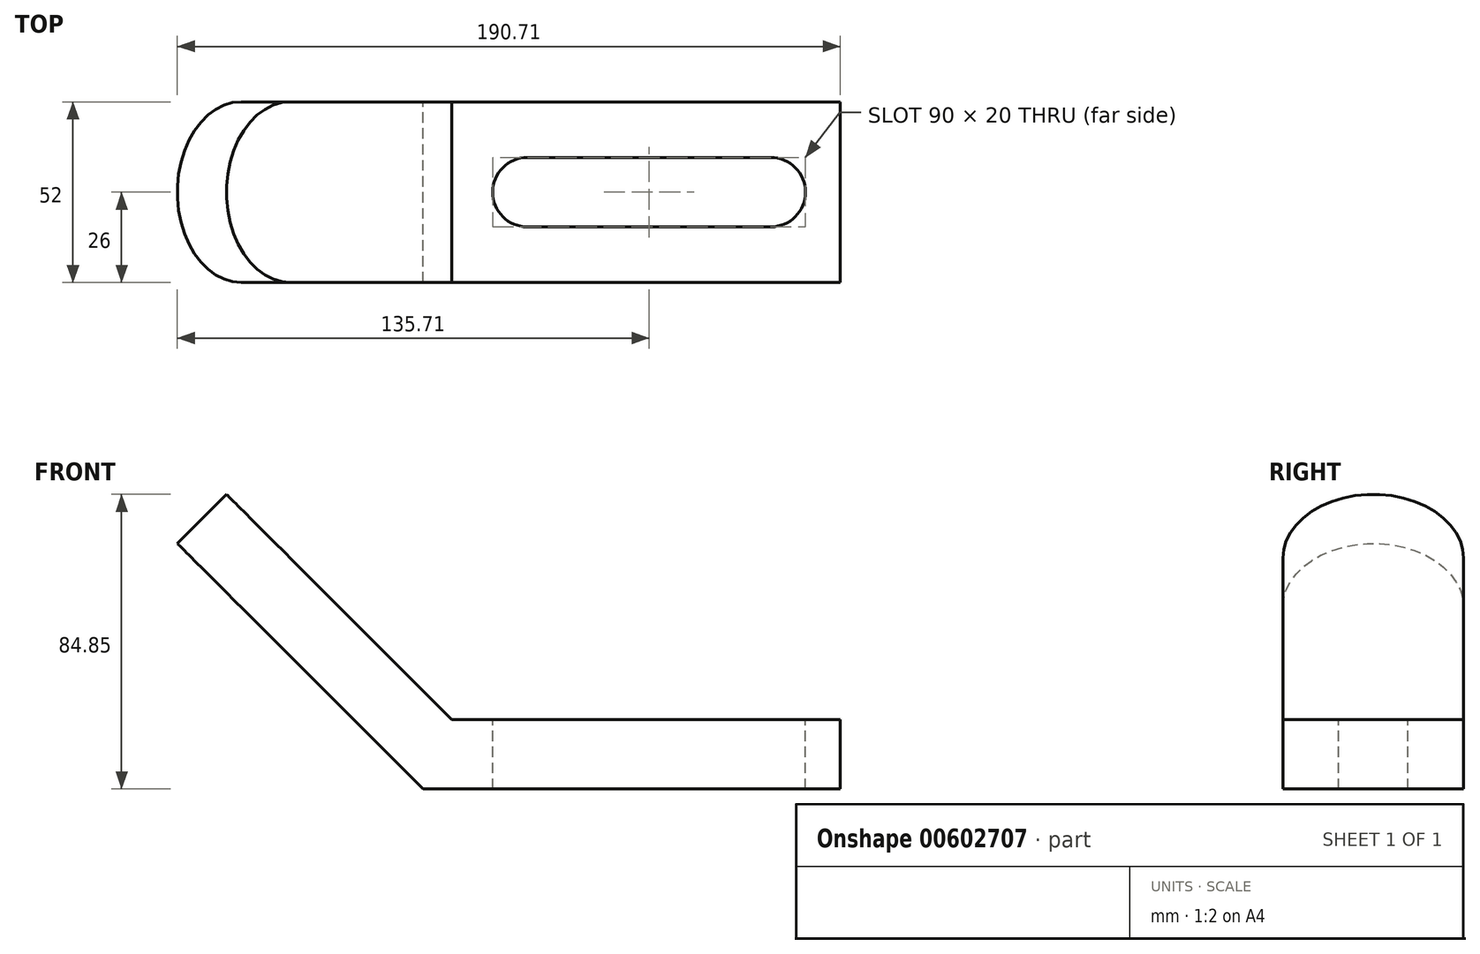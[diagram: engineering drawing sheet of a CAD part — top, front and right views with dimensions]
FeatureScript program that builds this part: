
annotation { "Feature Type Name" : "Feature", "Feature Type Description" : "" }
export const myFeature = defineFeature(function(context is Context, id is Id, definition is map)
    precondition{}
    {
        {
            var Q0;
            Q0=qCreatedBy(makeId("Front.planeOp"),FACE);
            var sketch = newSketch(context, id + "F0", { "sketchPlane" : qUnion([Q0])});
            skLineSegment(sketch, "E0", {"start": v(0, 0) * mm, "end": v(120, 0) * mm});
            skLineSegment(sketch, "E1", {"start": v(0, 0) * mm, "end": v(-70.71, 70.71) * mm});
            skLineSegment(sketch, "E2", {"start": v(-70.71, 70.71) * mm, "end": v(-56.57, 84.85) * mm});
            skLineSegment(sketch, "E3", {"start": v(-56.57, 84.85) * mm, "end": v(8.28, 20) * mm});
            skLineSegment(sketch, "E4", {"start": v(120, 0) * mm, "end": v(120, 20) * mm});
            skLineSegment(sketch, "E5", {"start": v(120, 20) * mm, "end": v(8.28, 20) * mm});
            skLineSegment(sketch, "E6", {"start": v(-45.25, 73.54) * mm, "end": v(-59.4, 59.4) * mm});
            skLineSegment(sketch, "E7", {"start": v(-31.11, 59.4) * mm, "end": v(-45.25, 45.25) * mm});
            skLineSegment(sketch, "E8", {"start": v(20, 20) * mm, "end": v(20, 0) * mm});
            skLineSegment(sketch, "E9", {"start": v(110, 20) * mm, "end": v(110, 0) * mm});
            skSolve(sketch);
        }
        {
            var Q0;
            Q0 = qSketchRegion(id + "F0", true);
            extrude(context, id + "F1", {"entities" : qUnion([Q0]), "depth" : 52 * mm, "offsetDistance" : 25 * mm});
        }
        {
            var Q0;
            Q0=makeQuery(id+"F1.opExtrude","CAP_EDGE",EDGE,{"disambiguationData":[OSD([sQuery(id+"F0.wireOp",EDGE,"E2")])],"isStart":true});
            var Q1;
            Q1=makeQuery(id+"F1.opExtrude","CAP_EDGE",EDGE,{"disambiguationData":[OSD([sQuery(id+"F0.wireOp",EDGE,"E2")])],"isStart":false});
            fillet(context, id + "F2", {"entities" : qUnion([Q0, Q1]), "radius" : 26 * mm, "tangentPropagation" : true, "allowEdgeOverflow" : false});
        }
        {
            var Q0;
            Q0=makeQuery(id+"F1.opExtrude","SWEPT_FACE",FACE,{"disambiguationData":[OSD([sQuery(id+"F0.wireOp",EDGE,"E3")])]});
            var sketch = newSketch(context, id + "F3", { "sketchPlane" : qUnion([Q0])});
            skLineSegment(sketch, "E10", {"start": v(-100, -26) * mm, "end": v(-84, -26) * mm});
            skCircle(sketch, "E11", {"center": v(-74, -26) * mm, "radius": 10 * mm});
            skSolve(sketch);
        }
        {
            var Q0;
            Q0 = qSketchRegion(id + "F3", true);
            extrude(context, id + "F4", {"entities" : qUnion([Q0]), "operationType" : NewBodyOperationType.REMOVE, "oppositeDirection" : true, "depth" : 25 * mm, "offsetDistance" : 25 * mm});
        }
        {
            var Q0;
            Q0=makeQuery(id+"F1.opExtrude","SWEPT_FACE",FACE,{"disambiguationData":[OSD([sQuery(id+"F0.wireOp",EDGE,"E5")])]});
            var sketch = newSketch(context, id + "F5", { "sketchPlane" : qUnion([Q0])});
            skLineSegment(sketch, "E12", {"start": v(30, -16) * mm, "end": v(100, -16) * mm});
            skLineSegment(sketch, "E13", {"start": v(110, -26) * mm, "end": v(110, -26) * mm});
            skLineSegment(sketch, "E14", {"start": v(100, -36) * mm, "end": v(30, -36) * mm});
            skLineSegment(sketch, "E15", {"start": v(20, -26) * mm, "end": v(20, -26) * mm});
            skPoint(sketch, "E16.visualSharp", {"position": v(110, -16) * mm});
            skArc(sketch, "E16.filletArc", {"start": v(110, -26) * mm, "mid": v(107.07, -18.93) * mm, "end": v(100, -16) * mm});
            skPoint(sketch, "E17.visualSharp", {"position": v(110, -36) * mm});
            skArc(sketch, "E17.filletArc", {"start": v(100, -36) * mm, "mid": v(107.07, -33.07) * mm, "end": v(110, -26) * mm});
            skPoint(sketch, "E18.visualSharp", {"position": v(20, -16) * mm});
            skArc(sketch, "E18.filletArc", {"start": v(30, -16) * mm, "mid": v(22.93, -18.93) * mm, "end": v(20, -26) * mm});
            skPoint(sketch, "E19.visualSharp", {"position": v(20, -36) * mm});
            skArc(sketch, "E19.filletArc", {"start": v(20, -26) * mm, "mid": v(22.93, -33.07) * mm, "end": v(30, -36) * mm});
            skSolve(sketch);
        }
        {
            var Q0;
            Q0=makeQuery(id+"F5.imprint","IMPRINT",FACE,{"disambiguationData":[TD([[makeQuery(id+"F5.imprint","IMPRINT",EDGE,{"derivedFrom":sQuery(id+"F5.wireOp",EDGE,"E12")}),-1.0]])]});
            extrude(context, id + "F6", {"entities" : qUnion([Q0]), "operationType" : NewBodyOperationType.REMOVE, "oppositeDirection" : true, "depth" : 25 * mm, "offsetDistance" : 25 * mm});
        }
    });
